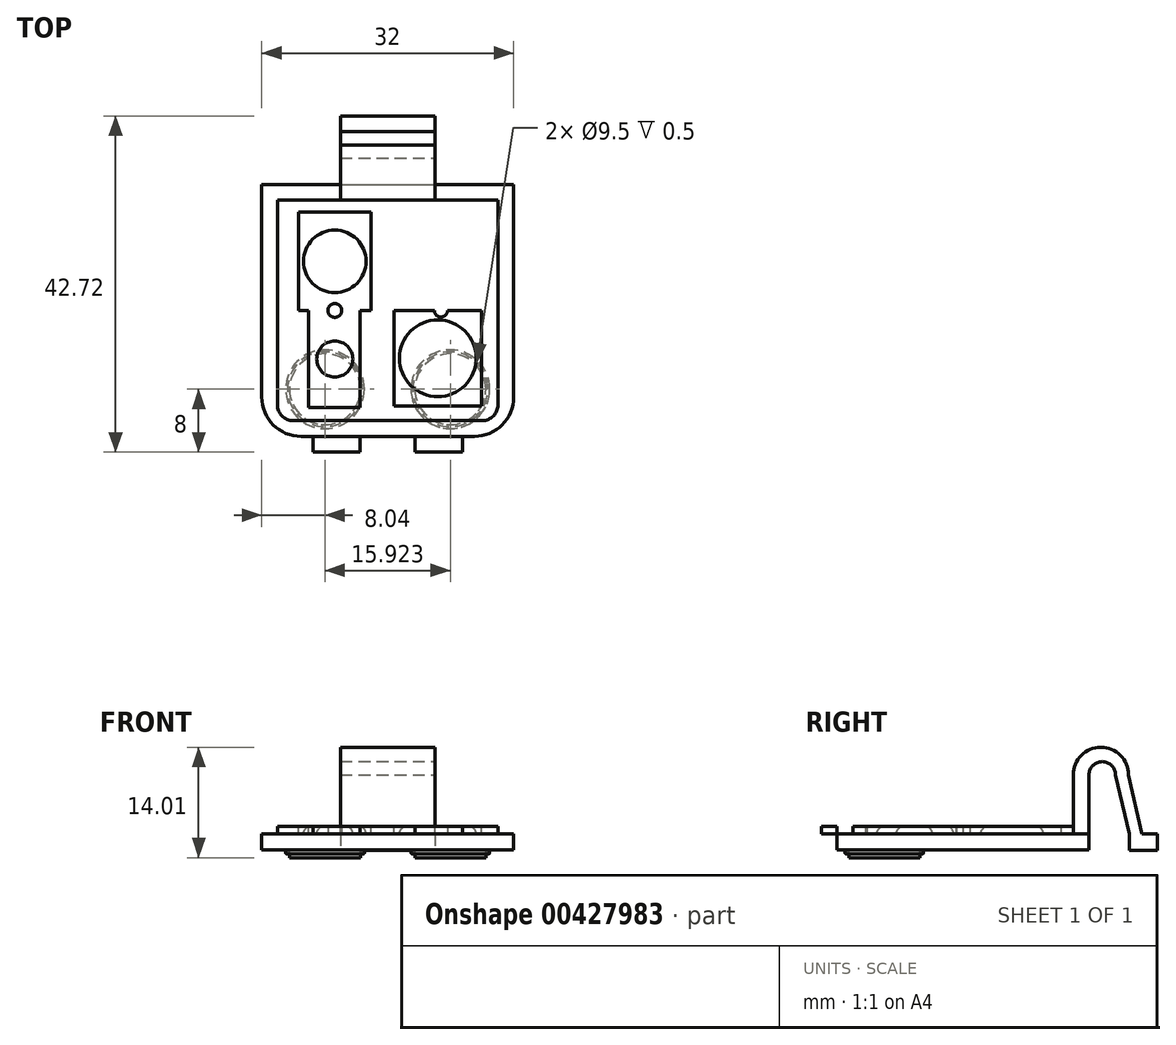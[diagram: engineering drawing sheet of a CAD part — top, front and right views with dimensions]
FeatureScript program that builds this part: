
annotation { "Feature Type Name" : "Feature", "Feature Type Description" : "" }
export const myFeature = defineFeature(function(context is Context, id is Id, definition is map)
    precondition{}
    {
        {
            var Q0;
            Q0=qCreatedBy(makeId("Top.planeOp"),FACE);
            var sketch = newSketch(context, id + "F0", { "sketchPlane" : qUnion([Q0])});
            skLineSegment(sketch, "E0.bottom", {"start": v(-16, 16) * mm, "end": v(16, 16) * mm});
            skLineSegment(sketch, "E0.top", {"start": v(-16, -16) * mm, "end": v(16, -16) * mm});
            skLineSegment(sketch, "E0.left", {"start": v(-16, 16) * mm, "end": v(-16, -16) * mm});
            skLineSegment(sketch, "E0.right", {"start": v(16, 16) * mm, "end": v(16, -16) * mm});
            skPoint(sketch, "E0.middle", {"position": v(0, 0) * mm});
            skSolve(sketch);
        }
        {
            var Q0;
            Q0=makeQuery(id+"F0.imprint","IMPRINT",FACE,{"disambiguationData":[TD([[makeQuery(id+"F0.imprint","IMPRINT",EDGE,{"derivedFrom":sQuery(id+"F0.wireOp",EDGE,"E0.bottom")}),-1.0]])]});
            extrude(context, id + "F1", {"entities" : qUnion([Q0]), "oppositeDirection" : true, "depth" : 2 * mm});
        }
        {
            var Q0;
            Q0=makeQuery(id+"F1.opExtrude","CAP_FACE",FACE,{"disambiguationData":[OSD([sQuery(id+"F0.wireOp",EDGE,"E0.bottom"),sQuery(id+"F0.wireOp",EDGE,"E0.top"),sQuery(id+"F0.wireOp",EDGE,"E0.left"),sQuery(id+"F0.wireOp",EDGE,"E0.right")])],"isStart":true});
            var sketch = newSketch(context, id + "F2", { "sketchPlane" : qUnion([Q0])});
            skLineSegment(sketch, "E1.bottom", {"start": v(-14, 14) * mm, "end": v(14, 14) * mm});
            skLineSegment(sketch, "E1.top", {"start": v(-14, -14) * mm, "end": v(14, -14) * mm});
            skLineSegment(sketch, "E1.left", {"start": v(-14, 14) * mm, "end": v(-14, -14) * mm});
            skLineSegment(sketch, "E1.right", {"start": v(14, 14) * mm, "end": v(14, -14) * mm});
            skPoint(sketch, "E1.middle", {"position": v(0, 0) * mm});
            skLineSegment(sketch, "E2.bottom", {"start": v(-9.5, -14) * mm, "end": v(-3.5, -14) * mm});
            skLineSegment(sketch, "E2.top", {"start": v(-9.5, -18) * mm, "end": v(-3.5, -18) * mm});
            skLineSegment(sketch, "E2.left", {"start": v(-9.5, -14) * mm, "end": v(-9.5, -18) * mm});
            skLineSegment(sketch, "E2.right", {"start": v(-3.5, -14) * mm, "end": v(-3.5, -18) * mm});
            skLineSegment(sketch, "E3.bottom", {"start": v(3.5, -14) * mm, "end": v(9.5, -14) * mm});
            skLineSegment(sketch, "E3.top", {"start": v(3.5, -18) * mm, "end": v(9.5, -18) * mm});
            skLineSegment(sketch, "E3.left", {"start": v(3.5, -14) * mm, "end": v(3.5, -18) * mm});
            skLineSegment(sketch, "E3.right", {"start": v(9.5, -14) * mm, "end": v(9.5, -18) * mm});
            skSolve(sketch);
        }
        {
            var Q0;
            Q0=makeQuery(id+"F2.imprint","IMPRINT",FACE,{"disambiguationData":[TD([[makeQuery(id+"F2.imprint","IMPRINT",EDGE,{"derivedFrom":sQuery(id+"F2.wireOp",EDGE,"E1.bottom")}),-1.0]])]});
            var Q1;
            {var subQ0=sQuery(id+"F2.wireOp",EDGE,"E3.top");Q1=makeQuery(id+"F2.imprint","IMPRINT",FACE,{"disambiguationData":[TD([[makeQuery(id+"F2.imprint","IMPRINT",EDGE,{"derivedFrom":subQ0}),1.0]])]});}
            var Q2;
            {var subQ0=sQuery(id+"F2.wireOp",EDGE,"E3.bottom");Q2=makeQuery(id+"F2.imprint","IMPRINT",FACE,{"disambiguationData":[TD([[makeQuery(id+"F2.imprint","IMPRINT",EDGE,{"derivedFrom":subQ0}),-1.0]])]});}
            var Q3;
            {var subQ0=sQuery(id+"F2.wireOp",EDGE,"E2.top");Q3=makeQuery(id+"F2.imprint","IMPRINT",FACE,{"disambiguationData":[TD([[makeQuery(id+"F2.imprint","IMPRINT",EDGE,{"derivedFrom":subQ0}),1.0]])]});}
            var Q4;
            {var subQ0=sQuery(id+"F2.wireOp",EDGE,"E2.bottom");Q4=makeQuery(id+"F2.imprint","IMPRINT",FACE,{"disambiguationData":[TD([[makeQuery(id+"F2.imprint","IMPRINT",EDGE,{"derivedFrom":subQ0}),-1.0]])]});}
            extrude(context, id + "F3", {"entities" : qUnion([Q0, Q1, Q2, Q3, Q4]), "operationType" : NewBodyOperationType.ADD, "depth" : 1 * mm});
        }
        {
            var Q0;
            Q0=makeQuery(id+"F1.opExtrude","SWEPT_EDGE",EDGE,{"disambiguationData":[OSD([sQuery(id+"F0.wireOp",EDGE,"E0.top"),sQuery(id+"F0.wireOp",EDGE,"E0.left")])]});
            var Q1;
            Q1=makeQuery(id+"F1.opExtrude","SWEPT_EDGE",EDGE,{"disambiguationData":[OSD([sQuery(id+"F0.wireOp",EDGE,"E0.top"),sQuery(id+"F0.wireOp",EDGE,"E0.right")])]});
            fillet(context, id + "F4", {"entities" : qUnion([Q0, Q1]), "radius" : 5 * mm, "tangentPropagation" : true, "allowEdgeOverflow" : false});
        }
        {
            var Q0;
            Q0=makeQuery(id+"F3.opExtrude","SWEPT_EDGE",EDGE,{"disambiguationData":[OSD([sQuery(id+"F2.wireOp",EDGE,"E1.top"),sQuery(id+"F2.wireOp",EDGE,"E1.left")])]});
            var Q1;
            Q1=makeQuery(id+"F3.opExtrude","SWEPT_EDGE",EDGE,{"disambiguationData":[OSD([sQuery(id+"F2.wireOp",EDGE,"E1.top"),sQuery(id+"F2.wireOp",EDGE,"E1.right")])]});
            fillet(context, id + "F5", {"entities" : qUnion([Q0, Q1]), "radius" : 2 * mm, "tangentPropagation" : true, "allowEdgeOverflow" : false});
        }
        {
            var Q0;
            Q0=makeQuery(id+"F1.opExtrude","CAP_FACE",FACE,{"disambiguationData":[OSD([sQuery(id+"F0.wireOp",EDGE,"E0.bottom"),sQuery(id+"F0.wireOp",EDGE,"E0.top"),sQuery(id+"F0.wireOp",EDGE,"E0.left"),sQuery(id+"F0.wireOp",EDGE,"E0.right")])],"isStart":false});
            var sketch = newSketch(context, id + "F6", { "sketchPlane" : qUnion([Q0])});
            skLineSegment(sketch, "E4.bottom", {"start": v(-15, 4) * mm, "end": v(15, 4) * mm});
            skLineSegment(sketch, "E4.top", {"start": v(-15, -15) * mm, "end": v(15, -15) * mm});
            skLineSegment(sketch, "E4.left", {"start": v(-15, 4) * mm, "end": v(-15, -15) * mm});
            skLineSegment(sketch, "E4.right", {"start": v(15, 4) * mm, "end": v(15, -15) * mm});
            skCircle(sketch, "E5", {"center": v(-7.96, 10) * mm, "radius": 5 * mm});
            skCircle(sketch, "E6", {"center": v(7.96, 10) * mm, "radius": 5 * mm});
            skLineSegment(sketch, "E7", {"start": v(-7.96, 10) * mm, "end": v(7.96, 10) * mm});
            skCircle(sketch, "E8", {"center": v(-7.96, 10) * mm, "radius": 4.75 * mm});
            skCircle(sketch, "E9", {"center": v(7.96, 10) * mm, "radius": 4.75 * mm});
            skCircle(sketch, "E10", {"center": v(-7.96, 10) * mm, "radius": 4.5 * mm});
            skCircle(sketch, "E11", {"center": v(7.96, 10) * mm, "radius": 4.5 * mm});
            skSolve(sketch);
        }
        {
            var Q0;
            Q0=makeQuery(id+"F6.imprint","IMPRINT",FACE,{"disambiguationData":[TD([[makeQuery(id+"F6.imprint","IMPRINT",EDGE,{"derivedFrom":sQuery(id+"F6.wireOp",EDGE,"E5")}),1.0]])]});
            var Q1;
            Q1=makeQuery(id+"F6.imprint","IMPRINT",FACE,{"disambiguationData":[TD([[makeQuery(id+"F6.imprint","IMPRINT",EDGE,{"derivedFrom":sQuery(id+"F6.wireOp",EDGE,"E6")}),1.0]])]});
            extrude(context, id + "F7", {"entities" : qUnion([Q0, Q1]), "operationType" : NewBodyOperationType.ADD, "depth" : 0.5 * mm});
        }
        {
            var Q0;
            Q0=makeQuery(id+"F6.imprint","IMPRINT",FACE,{"disambiguationData":[TD([[makeQuery(id+"F6.imprint","IMPRINT",EDGE,{"derivedFrom":sQuery(id+"F6.wireOp",EDGE,"E10")}),1.0]])]});
            var Q1;
            Q1=makeQuery(id+"F6.imprint","IMPRINT",FACE,{"disambiguationData":[TD([[makeQuery(id+"F6.imprint","IMPRINT",EDGE,{"derivedFrom":sQuery(id+"F6.wireOp",EDGE,"E11")}),1.0]])]});
            extrude(context, id + "F8", {"entities" : qUnion([Q0, Q1]), "operationType" : NewBodyOperationType.ADD, "depth" : 1 * mm});
        }
        {
            var Q0;
            Q0=makeQuery(id+"F7.opExtrude","CAP_EDGE",EDGE,{"disambiguationData":[OSD([sQuery(id+"F6.wireOp",EDGE,"E5")])],"isStart":false});
            fillet(context, id + "F9", {"entities" : qUnion([Q0]), "radius" : 0.1 * mm, "tangentPropagation" : true, "allowEdgeOverflow" : false});
        }
        {
            var Q0;
            Q0=makeQuery(id+"F7.opExtrude","CAP_EDGE",EDGE,{"disambiguationData":[OSD([sQuery(id+"F6.wireOp",EDGE,"E6")])],"isStart":false});
            fillet(context, id + "F10", {"entities" : qUnion([Q0]), "radius" : 0.1 * mm, "tangentPropagation" : true, "allowEdgeOverflow" : false});
        }
        {
            var Q0;
            Q0=makeQuery(id+"F3.opExtrude","CAP_FACE",FACE,{"disambiguationData":[OSD([sQuery(id+"F2.wireOp",EDGE,"E1.bottom"),sQuery(id+"F2.wireOp",EDGE,"E1.top"),sQuery(id+"F2.wireOp",EDGE,"E1.left"),sQuery(id+"F2.wireOp",EDGE,"E1.right"),sQuery(id+"F2.wireOp",EDGE,"E2.top"),sQuery(id+"F2.wireOp",EDGE,"E2.left"),sQuery(id+"F2.wireOp",EDGE,"E2.right"),sQuery(id+"F2.wireOp",EDGE,"E3.top"),sQuery(id+"F2.wireOp",EDGE,"E3.left"),sQuery(id+"F2.wireOp",EDGE,"E3.right")])],"isStart":false});
            var sketch = newSketch(context, id + "F11", { "sketchPlane" : qUnion([Q0])});
            skLineSegment(sketch, "E12.bottom", {"start": v(-3.5, -12.34) * mm, "end": v(-10.05, -12.34) * mm});
            skLineSegment(sketch, "E12.top", {"start": v(-3.5, 0) * mm, "end": v(-10.05, 0) * mm});
            skLineSegment(sketch, "E12.left", {"start": v(-3.5, -12.34) * mm, "end": v(-3.5, 0) * mm});
            skLineSegment(sketch, "E12.right", {"start": v(-10.05, -12.34) * mm, "end": v(-10.05, 0) * mm});
            skLineSegment(sketch, "E13.bottom", {"start": v(-3.5, 0) * mm, "end": v(-7.36, 0) * mm});
            skLineSegment(sketch, "E14.bottom", {"start": v(-2.13, 0) * mm, "end": v(-11.31, 0) * mm});
            skLineSegment(sketch, "E14.top", {"start": v(-2.13, 12.48) * mm, "end": v(-11.31, 12.48) * mm});
            skLineSegment(sketch, "E14.left", {"start": v(-2.13, 0) * mm, "end": v(-2.13, 12.48) * mm});
            skLineSegment(sketch, "E14.right", {"start": v(-11.31, 0) * mm, "end": v(-11.31, 12.48) * mm});
            skLineSegment(sketch, "E15.bottom", {"start": v(0.8, -12.13) * mm, "end": v(11.93, -12.13) * mm});
            skLineSegment(sketch, "E15.top", {"start": v(0.8, 0) * mm, "end": v(11.93, 0) * mm});
            skLineSegment(sketch, "E15.left", {"start": v(0.8, -12.13) * mm, "end": v(0.8, 0) * mm});
            skLineSegment(sketch, "E15.right", {"start": v(11.93, -12.13) * mm, "end": v(11.93, 0) * mm});
            skLineSegment(sketch, "E16.bottom", {"start": v(3.5, 0) * mm, "end": v(10.37, 0) * mm});
            skLineSegment(sketch, "E16.top", {"start": v(3.5, 12.48) * mm, "end": v(10.37, 12.48) * mm});
            skLineSegment(sketch, "E16.left", {"start": v(3.5, 0) * mm, "end": v(3.5, 12.48) * mm});
            skLineSegment(sketch, "E16.right", {"start": v(10.37, 0) * mm, "end": v(10.37, 12.48) * mm});
            skSolve(sketch);
        }
        {
            var Q0;
            Q0=makeQuery(id+"F11.imprint","IMPRINT",FACE,{"disambiguationData":[TD([[makeQuery(id+"F11.imprint","IMPRINT",EDGE,{"derivedFrom":sQuery(id+"F11.wireOp",EDGE,"E12.bottom")}),-1.0]])]});
            var Q1;
            Q1=makeQuery(id+"F11.imprint","IMPRINT",FACE,{"disambiguationData":[TD([[makeQuery(id+"F11.imprint","IMPRINT",EDGE,{"derivedFrom":sQuery(id+"F11.wireOp",EDGE,"E14.top")}),1.0]])]});
            var Q2;
            Q2=makeQuery(id+"F11.imprint","IMPRINT",FACE,{"disambiguationData":[TD([[makeQuery(id+"F11.imprint","IMPRINT",EDGE,{"derivedFrom":sQuery(id+"F11.wireOp",EDGE,"E16.bottom")}),1.0]])]});
            var Q3;
            Q3=makeQuery(id+"F11.imprint","IMPRINT",FACE,{"disambiguationData":[TD([[makeQuery(id+"F11.imprint","IMPRINT",EDGE,{"derivedFrom":sQuery(id+"F11.wireOp",EDGE,"E15.bottom")}),1.0]])]});
            extrude(context, id + "F12", {"entities" : qUnion([Q0, Q1, Q2, Q3]), "operationType" : NewBodyOperationType.REMOVE, "oppositeDirection" : true, "depth" : 1 * mm});
        }
        {
            var Q0;
            Q0=makeQuery(id+"F12.boolean.opBoolean","COPY",FACE,{"derivedFrom":makeQuery(id+"F12.opExtrude","CAP_FACE",FACE,{"disambiguationData":[OSD([sQuery(id+"F11.wireOp",EDGE,"E12.bottom"),sQuery(id+"F11.wireOp",EDGE,"E12.left"),sQuery(id+"F11.wireOp",EDGE,"E12.right"),sQuery(id+"F11.wireOp",EDGE,"E14.bottom"),sQuery(id+"F11.wireOp",EDGE,"E14.top"),sQuery(id+"F11.wireOp",EDGE,"E14.left"),sQuery(id+"F11.wireOp",EDGE,"E14.right")])],"isStart":false})});
            var sketch = newSketch(context, id + "F13", { "sketchPlane" : qUnion([Q0])});
            skCircle(sketch, "E17", {"center": v(-6.72, -6.17) * mm, "radius": 2.3 * mm});
            skPoint(sketch, "E17.centerSnap0", {"position": v(-6.72, 12.48) * mm});
            skPoint(sketch, "E17.centerSnap1", {"position": v(-10.05, -6.17) * mm});
            skCircle(sketch, "E18", {"center": v(-6.72, 6.24) * mm, "radius": 3.97 * mm});
            skPoint(sketch, "E18.centerSnap0", {"position": v(-11.31, 6.24) * mm});
            skCircle(sketch, "E19", {"center": v(-6.72, 0) * mm, "radius": 0.88 * mm});
            skSolve(sketch);
        }
        {
            var Q0;
            Q0=makeQuery(id+"F13.imprint","IMPRINT",FACE,{"disambiguationData":[TD([[makeQuery(id+"F13.imprint","IMPRINT",EDGE,{"derivedFrom":sQuery(id+"F13.wireOp",EDGE,"E18")}),1.0]])]});
            var Q1;
            Q1=makeQuery(id+"F13.imprint","IMPRINT",FACE,{"disambiguationData":[TD([[makeQuery(id+"F13.imprint","IMPRINT",EDGE,{"derivedFrom":sQuery(id+"F13.wireOp",EDGE,"E19")}),1.0]])]});
            var Q2;
            Q2=makeQuery(id+"F13.imprint","IMPRINT",FACE,{"disambiguationData":[TD([[makeQuery(id+"F13.imprint","IMPRINT",EDGE,{"derivedFrom":sQuery(id+"F13.wireOp",EDGE,"E17")}),1.0]])]});
            var Q3;
            Q3=sQuery(id+"F13.wireOp",EDGE,"E18");
            extrude(context, id + "F14", {"entities" : qUnion([Q0, Q1, Q2]), "operationType" : NewBodyOperationType.ADD, "surfaceEntities" : qUnion([Q3]), "depth" : 1 * mm});
        }
        {
            var Q0;
            Q0=makeQuery(id+"F14.opExtrude","CAP_EDGE",EDGE,{"disambiguationData":[OSD([sQuery(id+"F13.wireOp",EDGE,"E18")])],"isStart":false});
            var Q1;
            Q1=makeQuery(id+"F14.opExtrude","CAP_EDGE",EDGE,{"disambiguationData":[OSD([sQuery(id+"F13.wireOp",EDGE,"E17")])],"isStart":false});
            fillet(context, id + "F15", {"entities" : qUnion([Q0, Q1]), "radius" : 1 * mm, "tangentPropagation" : true, "allowEdgeOverflow" : false});
        }
        {
            var Q0;
            Q0=makeQuery(id+"F12.boolean.opBoolean","COPY",FACE,{"derivedFrom":makeQuery(id+"F12.opExtrude","CAP_FACE",FACE,{"disambiguationData":[OSD([sQuery(id+"F11.wireOp",EDGE,"E15.bottom"),sQuery(id+"F11.wireOp",EDGE,"E15.top"),sQuery(id+"F11.wireOp",EDGE,"E15.left"),sQuery(id+"F11.wireOp",EDGE,"E15.right"),sQuery(id+"F11.wireOp",EDGE,"E16.top"),sQuery(id+"F11.wireOp",EDGE,"E16.left"),sQuery(id+"F11.wireOp",EDGE,"E16.right")])],"isStart":false})});
            var sketch = newSketch(context, id + "F16", { "sketchPlane" : qUnion([Q0])});
            skCircle(sketch, "E20", {"center": v(6.37, -6.06) * mm, "radius": 4.87 * mm});
            skPoint(sketch, "E20.centerSnap0", {"position": v(11.93, -6.06) * mm});
            skPoint(sketch, "E20.centerSnap1", {"position": v(6.37, -12.13) * mm});
            skCircle(sketch, "E21", {"center": v(6.93, 6.24) * mm, "radius": 2.77 * mm});
            skPoint(sketch, "E21.centerSnap0", {"position": v(6.93, 12.48) * mm});
            skPoint(sketch, "E21.centerSnap1", {"position": v(3.5, 6.24) * mm});
            skCircle(sketch, "E22", {"center": v(6.76, 0) * mm, "radius": 0.84 * mm});
            skSolve(sketch);
        }
        {
            var Q0;
            Q0=makeQuery(id+"F16.imprint","IMPRINT",FACE,{"disambiguationData":[TD([[makeQuery(id+"F16.imprint","IMPRINT",EDGE,{"derivedFrom":sQuery(id+"F16.wireOp",EDGE,"E21")}),1.0]])]});
            var Q1;
            Q1=makeQuery(id+"F16.imprint","IMPRINT",FACE,{"disambiguationData":[TD([[makeQuery(id+"F16.imprint","IMPRINT",EDGE,{"derivedFrom":sQuery(id+"F16.wireOp",EDGE,"E22")}),1.0]])]});
            var Q2;
            Q2=makeQuery(id+"F16.imprint","IMPRINT",FACE,{"disambiguationData":[TD([[makeQuery(id+"F16.imprint","IMPRINT",EDGE,{"derivedFrom":sQuery(id+"F16.wireOp",EDGE,"E20")}),1.0]])]});
            extrude(context, id + "F17", {"entities" : qUnion([Q0, Q1, Q2]), "operationType" : NewBodyOperationType.ADD, "depth" : 1 * mm});
        }
        {
            var Q0;
            Q0=makeQuery(id+"F17.opExtrude","CAP_EDGE",EDGE,{"disambiguationData":[OSD([sQuery(id+"F16.wireOp",EDGE,"E21")])],"isStart":false});
            var Q1;
            Q1=makeQuery(id+"F17.opExtrude","CAP_EDGE",EDGE,{"disambiguationData":[OSD([sQuery(id+"F16.wireOp",EDGE,"E20")])],"isStart":false});
            fillet(context, id + "F18", {"entities" : qUnion([Q0, Q1]), "radius" : 1 * mm, "tangentPropagation" : true, "allowEdgeOverflow" : false});
        }
        {
            var Q0;
            Q0=qCreatedBy(makeId("Right.planeOp"),FACE);
            cPlane(context, id + "F19", {"entities" : qUnion([Q0]), "cplaneType" : CPlaneType.OFFSET, "offset" : 6 * mm, "width" : 152.4 * mm, "height" : 152.4 * mm});
        }
        {
            var Q0;
            Q0=qCreatedBy(id+"F19.planeOp",FACE);
            var sketch = newSketch(context, id + "F20", { "sketchPlane" : qUnion([Q0])});
            skLineSegment(sketch, "E23.bottom", {"start": v(14, 0) * mm, "end": v(16, 0) * mm});
            skLineSegment(sketch, "E23.top", {"start": v(14, 7.5) * mm, "end": v(16, 7.5) * mm});
            skLineSegment(sketch, "E23.left", {"start": v(14, 0) * mm, "end": v(14, 7.5) * mm});
            skLineSegment(sketch, "E23.right", {"start": v(16, 0) * mm, "end": v(16, 7.5) * mm});
            skArc(sketch, "E24", {"start": v(19.39, 7.5) * mm, "mid": v(17.7, 9.2) * mm, "end": v(16, 7.5) * mm});
            skArc(sketch, "E25", {"start": v(21.03, 7.5) * mm, "mid": v(17.51, 11.01) * mm, "end": v(14, 7.5) * mm});
            skPoint(sketch, "E25.startSnap0", {"position": v(15, 7.5) * mm});
            skLineSegment(sketch, "E26", {"start": v(19.39, 7.5) * mm, "end": v(21.1, 0) * mm});
            skLineSegment(sketch, "E27", {"start": v(21.1, 0) * mm, "end": v(22.75, 0) * mm});
            skLineSegment(sketch, "E28", {"start": v(22.75, 0) * mm, "end": v(21.03, 7.5) * mm});
            skLineSegment(sketch, "E29.bottom", {"start": v(21.1, 0) * mm, "end": v(24.72, 0) * mm});
            skLineSegment(sketch, "E29.top", {"start": v(21.1, -2.09) * mm, "end": v(24.72, -2.09) * mm});
            skLineSegment(sketch, "E29.left", {"start": v(21.1, 0) * mm, "end": v(21.1, -2.09) * mm});
            skLineSegment(sketch, "E29.right", {"start": v(24.72, 0) * mm, "end": v(24.72, -2.09) * mm});
            skSolve(sketch);
        }
        {
            var Q0;
            Q0=makeQuery(id+"F20.imprint","IMPRINT",FACE,{"disambiguationData":[TD([[makeQuery(id+"F20.imprint","IMPRINT",EDGE,{"derivedFrom":sQuery(id+"F20.wireOp",EDGE,"E23.bottom")}),1.0]])]});
            var Q1;
            Q1=makeQuery(id+"F20.imprint","IMPRINT",FACE,{"disambiguationData":[TD([[makeQuery(id+"F20.imprint","IMPRINT",EDGE,{"derivedFrom":sQuery(id+"F20.wireOp",EDGE,"E23.top")}),1.0]])]});
            var Q2;
            Q2=makeQuery(id+"F20.imprint","IMPRINT",FACE,{"disambiguationData":[TD([[makeQuery(id+"F20.imprint","IMPRINT",EDGE,{"derivedFrom":sQuery(id+"F20.wireOp",EDGE,"E29.top")}),1.0]])]});
            extrude(context, id + "F21", {"entities" : qUnion([Q0, Q1, Q2]), "operationType" : NewBodyOperationType.ADD, "oppositeDirection" : true, "depth" : 12 * mm});
        }
    });
